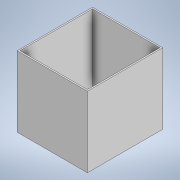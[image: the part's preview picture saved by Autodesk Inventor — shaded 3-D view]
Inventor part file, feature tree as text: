
AUTODESK INVENTOR PART (.ipt)
format: ipt  version: 2020 (Build 240168000, 168)  size: 233,472 bytes
history: native  units: mm
features: extrude x2, sketch x2
ambient origin geometry x8: Origin, YZ Plane, XZ Plane, XY Plane, X Axis, Y Axis, Z Axis, Center Point
bodies: Solid1 (feature_tree)
feature tree (4):
  extrude  "Extrusion1"  Depth=80.0mm
  extrude  "Extrusion2"  Depth=1.5mm
  sketch  "Sketch1"  dims[d0=74.5mm d1=80.0mm]
  sketch  "Sketch2"  dims[d2=75.0mm d3=0.0mm d4=1.5mm d5=1.5mm d6=1.5mm d7=1.5mm d8=73.5mm d9=0.0mm]
